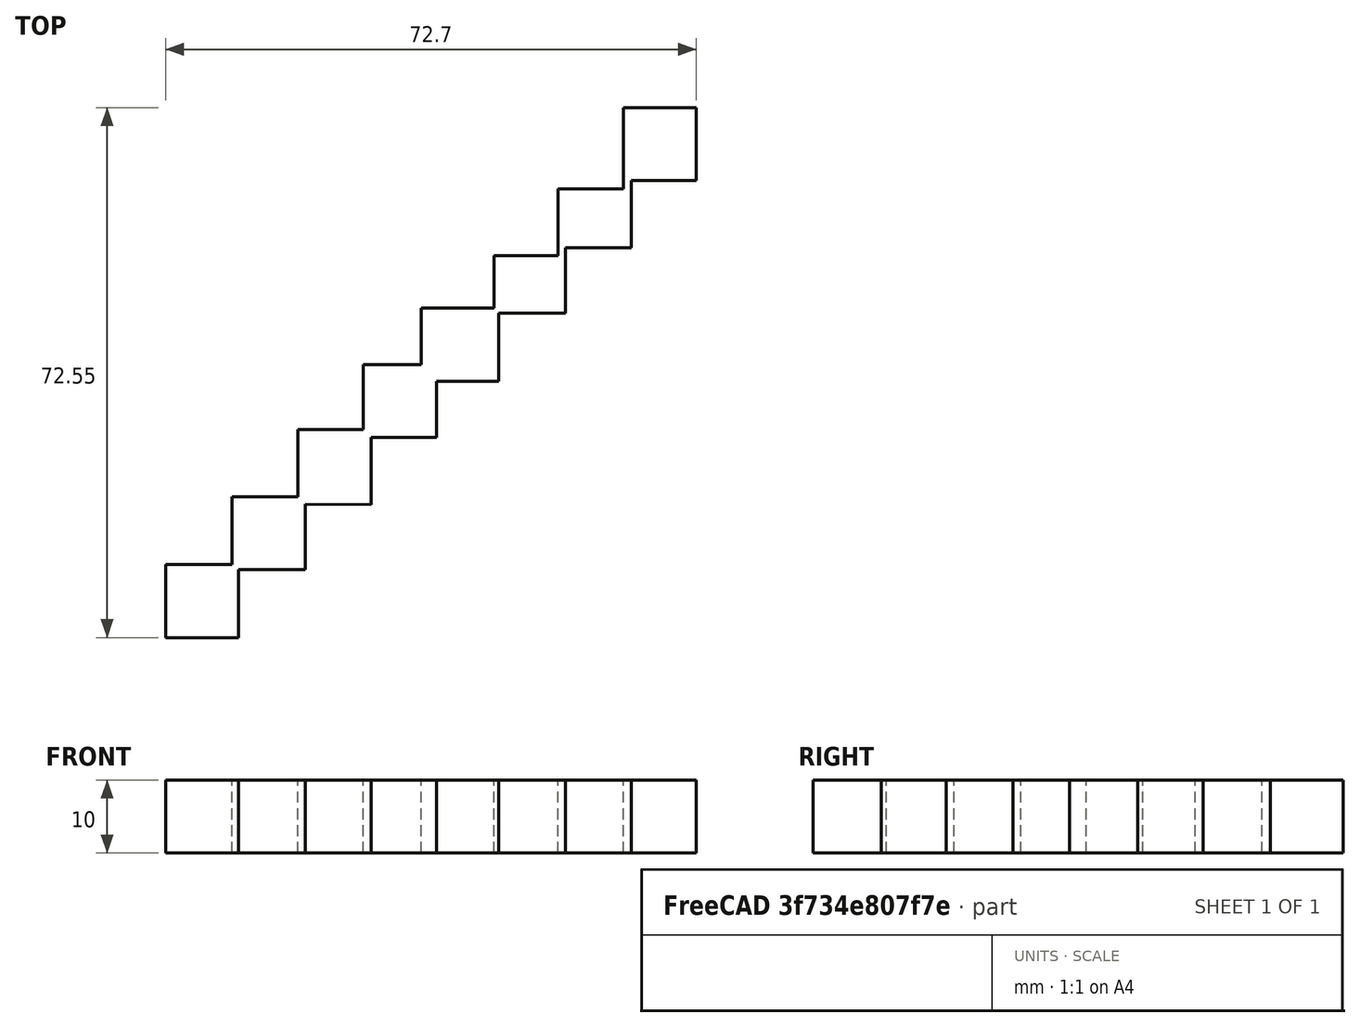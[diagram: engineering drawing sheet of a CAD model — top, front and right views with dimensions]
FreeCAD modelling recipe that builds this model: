
FCSTD DOCUMENT  (FreeCAD 0.19R24291 (Git))
Label: qwer
License: All rights reserved
LicenseURL: http://en.wikipedia.org/wiki/All_rights_reserved
objects: Sketcher::SketchObject×1, PartDesign::Pad×1, PartDesign::Body×1
note: 4 computed .brp shape members not serialized (recipe doc carries the construction recipe); baked Part::Feature solids carry a one-line shape summary decoded from their .brp

FEATURE [Sketcher::SketchObject] Sketch
  FullyConstrained = false
  MapMode = 5
  Support = -> [XY_Plane]
  sketch-geometry (32):
    g0: LineSegment StartX=-16.3959 StartY=15.1701 StartZ=0 EndX=-7.27594 EndY=15.1701 EndZ=0
    g1: LineSegment StartX=-16.3959 StartY=5.17014 StartZ=0 EndX=-16.3959 EndY=15.1701 EndZ=0
    g2: LineSegment StartX=-6.39592 StartY=14.4499 StartZ=0 EndX=-6.39592 EndY=5.17014 EndZ=0
    g3: LineSegment StartX=-16.3959 StartY=5.17014 StartZ=0 EndX=-6.39592 EndY=5.17014 EndZ=0
    g4: LineSegment StartX=-7.27594 StartY=24.4499 StartZ=0 EndX=1.74462 EndY=24.4499 EndZ=0
    g5: LineSegment StartX=-7.27594 StartY=15.1701 StartZ=0 EndX=-7.27594 EndY=24.4499 EndZ=0
    g6: LineSegment StartX=2.72406 StartY=23.4155 StartZ=0 EndX=2.72406 EndY=14.4499 EndZ=0
    g7: LineSegment StartX=-6.39592 StartY=14.4499 StartZ=0 EndX=2.72406 EndY=14.4499 EndZ=0
    g8: LineSegment StartX=1.74462 StartY=33.6244 StartZ=0 EndX=10.6829 EndY=33.6244 EndZ=0
    g9: LineSegment StartX=1.74462 StartY=24.4499 StartZ=0 EndX=1.74462 EndY=33.6244 EndZ=0
    g10: LineSegment StartX=11.7446 StartY=32.5399 StartZ=0 EndX=11.7446 EndY=23.3478 EndZ=0
    g11: LineSegment StartX=2.72406 StartY=23.4155 StartZ=0 EndX=11.7446 EndY=23.3478 EndZ=0
    g12: LineSegment StartX=10.6829 StartY=42.5399 StartZ=0 EndX=18.6152 EndY=42.5399 EndZ=0
    g13: LineSegment StartX=10.6829 StartY=33.6244 StartZ=0 EndX=10.6829 EndY=42.5399 EndZ=0
    g14: LineSegment StartX=20.6829 StartY=40.2829 StartZ=0 EndX=20.6829 EndY=32.5399 EndZ=0
    g15: LineSegment StartX=11.7446 StartY=32.5399 StartZ=0 EndX=20.6829 EndY=32.5399 EndZ=0
    g16: LineSegment StartX=29.2152 StartY=49.5629 StartZ=0 EndX=29.2152 EndY=40.2829 EndZ=0
    g17: LineSegment StartX=20.6829 StartY=40.2829 StartZ=0 EndX=29.2152 EndY=40.2829 EndZ=0
    g18: LineSegment StartX=38.3352 StartY=58.5329 StartZ=0 EndX=38.3352 EndY=49.5629 EndZ=0
    g19: LineSegment StartX=29.2152 StartY=49.5629 StartZ=0 EndX=38.3352 EndY=49.5629 EndZ=0
    g20: LineSegment StartX=18.6152 StartY=50.2829 StartZ=0 EndX=28.6152 EndY=50.2829 EndZ=0
    g21: LineSegment StartX=18.6152 StartY=42.5399 StartZ=0 EndX=18.6152 EndY=50.2829 EndZ=0
    g22: LineSegment StartX=28.6152 StartY=57.4436 StartZ=0 EndX=37.3552 EndY=57.4436 EndZ=0
    g23: LineSegment StartX=28.6152 StartY=50.2829 StartZ=0 EndX=28.6152 EndY=57.4436 EndZ=0
    g24: LineSegment StartX=37.3552 StartY=66.6181 StartZ=0 EndX=46.2952 EndY=66.6181 EndZ=0
    g25: LineSegment StartX=37.3552 StartY=57.4436 StartZ=0 EndX=37.3552 EndY=66.6181 EndZ=0
    g26: LineSegment StartX=47.3552 StartY=67.7229 StartZ=0 EndX=47.3552 EndY=58.5329 EndZ=0
    g27: LineSegment StartX=38.3352 StartY=58.5329 StartZ=0 EndX=47.3552 EndY=58.5329 EndZ=0
    g28: LineSegment StartX=47.3552 StartY=67.7229 StartZ=0 EndX=56.2952 EndY=67.7229 EndZ=0
    g29: LineSegment StartX=46.2952 StartY=77.7229 StartZ=0 EndX=56.2952 EndY=77.7229 EndZ=0
    g30: LineSegment StartX=46.2952 StartY=66.6181 StartZ=0 EndX=46.2952 EndY=77.7229 EndZ=0
    g31: LineSegment StartX=56.2952 StartY=77.7229 StartZ=0 EndX=56.2952 EndY=67.7229 EndZ=0
  constraints (70):
    c: Horizontal(g0)
    c: Vertical(g1)
    c: Coincident(g0,g1)
    c: Vertical(g2)
    c: Coincident(g3,g2)
    c: Coincident(g3,g1)
    c: Horizontal(g4)
    c: Vertical(g5)
    c: Coincident(g4,g5)
    c: Vertical(g6)
    c: Coincident(g7,g6)
    c: Coincident(g7,g2)
    c: Coincident(g5,g0)
    c: Horizontal(g8)
    c: Vertical(g9)
    c: Coincident(g8,g9)
    c: Vertical(g10)
    c: Coincident(g11,g10)
    c: Horizontal(g12)
    c: Vertical(g13)
    c: Coincident(g12,g13)
    c: Vertical(g14)
    c: Coincident(g15,g14)
    c: Horizontal(g15)
    c: Coincident(g11,g6)
    c: Coincident(g9,g4)
    c: Coincident(g15,g10)
    c: Coincident(g13,g8)
    c: Horizontal(g20)
    c: Vertical(g21)
    c: Coincident(g20,g21)
    c: Vertical(g16)
    c: Coincident(g17,g16)
    c: Horizontal(g22)
    c: Vertical(g23)
    c: Coincident(g22,g23)
    c: Vertical(g18)
    c: Coincident(g19,g18)
    c: Coincident(g19,g16)
    c: Coincident(g23,g20)
    c: Horizontal(g24)
    c: Vertical(g25)
    c: Coincident(g24,g25)
    c: Vertical(g26)
    c: Coincident(g27,g26)
    c: Horizontal(g29)
    c: Vertical(g30)
    c: Coincident(g29,g30)
    c: Equal(g29,g31) = 10
    c: Vertical(g31)
    c: Coincident(g31,g29)
    c: Coincident(g28,g31)
    c: Horizontal(g28)
    c: Coincident(g27,g18)
    c: Coincident(g25,g22)
    c: Coincident(g28,g26)
    c: Coincident(g30,g24)
    c: DistanceY(g16,g16) = 9.28
    c: DistanceX(g20,g20) = 10
    c: DistanceY(g18,g18) = 8.97
    c: DistanceY(g26,g26) = 9.19
    c: DistanceX(g24,g24) = 8.94
    c: DistanceX(g22,g22) = 8.74
    c: DistanceX(g19,g19) = 9.12
    c: DistanceX(g27,g27) = 9.02
    c: Horizontal(g17)
    c: Horizontal(g19)
    c: Horizontal(g27)
    c: Coincident(g17,g14)
    c: Coincident(g21,g12)
FEATURE [PartDesign::Pad] Pad
  Direction = (1,1,1)
  Length = 10
  Length2 = 100
  Profile = -> Sketch
  Type = 0
FEATURE [PartDesign::Body] Body
  Group = -> [Sketch,Pad]
  Origin = -> Origin
  Tip = -> Pad
